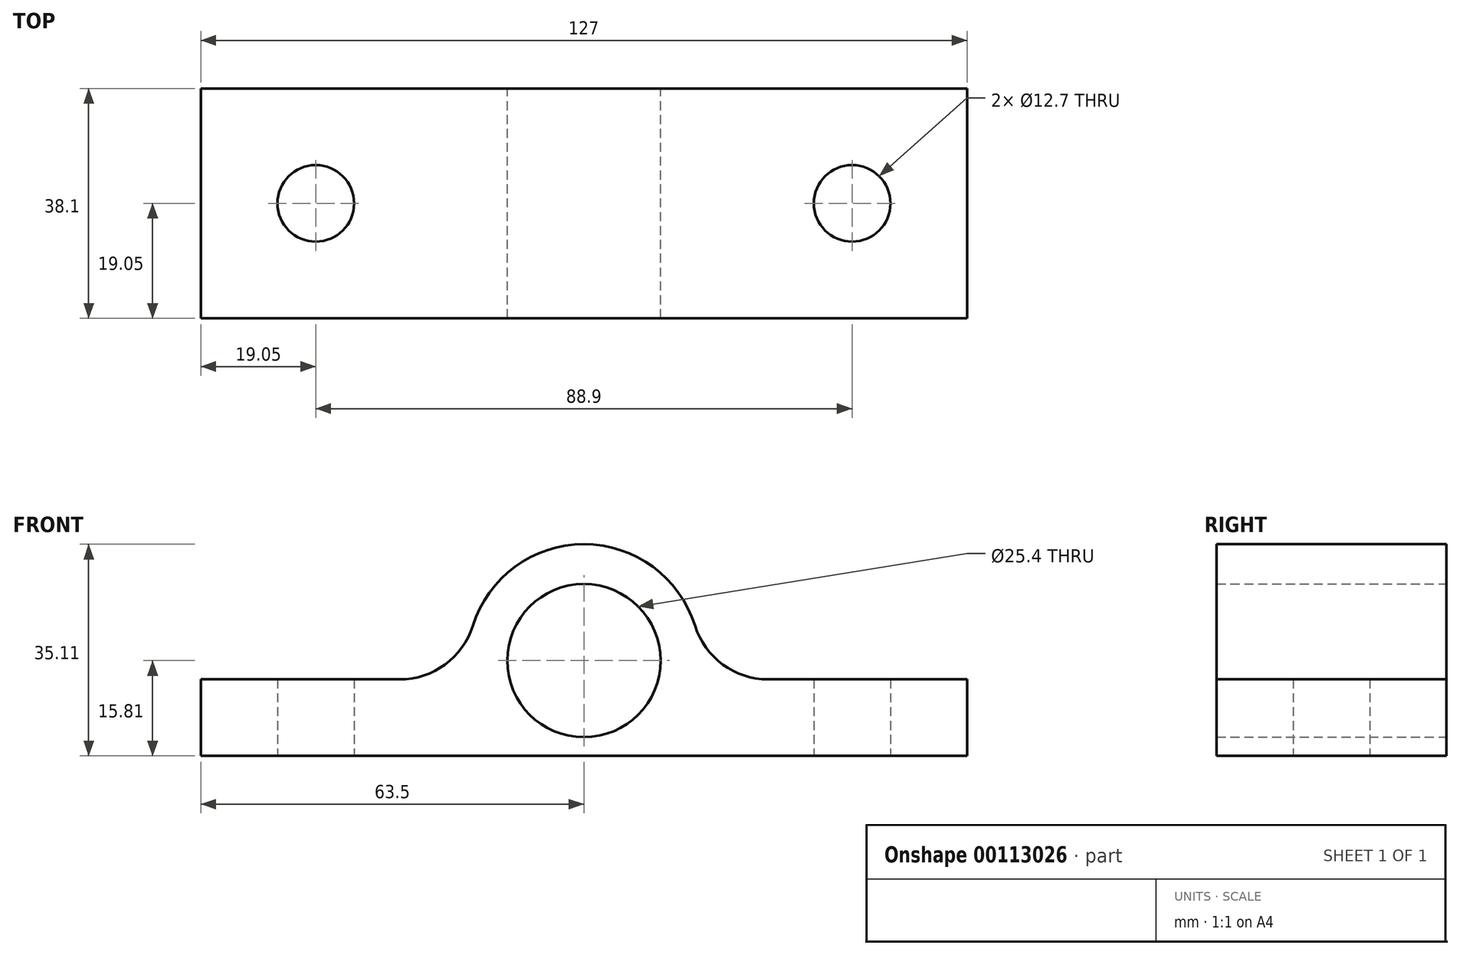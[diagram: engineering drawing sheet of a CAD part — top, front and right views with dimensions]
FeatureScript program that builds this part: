
annotation { "Feature Type Name" : "Feature", "Feature Type Description" : "" }
export const myFeature = defineFeature(function(context is Context, id is Id, definition is map)
    precondition{}
    {
        {
            var Q0;
            Q0=qCreatedBy(makeId("Front.planeOp"),FACE);
            var sketch = newSketch(context, id + "F0", { "sketchPlane" : qUnion([Q0])});
            skLineSegment(sketch, "E0", {"start": v(-63.5, 0) * mm, "end": v(63.5, 0) * mm});
            skLineSegment(sketch, "E1", {"start": v(63.5, 0) * mm, "end": v(63.5, 12.7) * mm});
            skLineSegment(sketch, "E2", {"start": v(63.5, 12.7) * mm, "end": v(19.05, 12.7) * mm});
            skLineSegment(sketch, "E3", {"start": v(-63.5, 0) * mm, "end": v(-63.5, 12.7) * mm});
            skLineSegment(sketch, "E4", {"start": v(-63.5, 12.7) * mm, "end": v(-19.05, 12.7) * mm});
            skArc(sketch, "E5", {"start": v(19.05, 12.7) * mm, "mid": v(0, 35.11) * mm, "end": v(-19.05, 12.7) * mm});
            skCircle(sketch, "E6", {"center": v(0, 15.81) * mm, "radius": 12.7 * mm});
            skSolve(sketch);
        }
        {
            var Q0;
            Q0=makeQuery(id+"F0.imprint","IMPRINT",FACE,{"disambiguationData":[TD([[makeQuery(id+"F0.imprint","IMPRINT",EDGE,{"derivedFrom":sQuery(id+"F0.wireOp",EDGE,"E0")}),1.0]])]});
            extrude(context, id + "F1", {"entities" : qUnion([Q0]), "endBound" : BoundingType.SYMMETRIC, "depth" : 38.1 * mm});
        }
        {
            var Q0;
            Q0=makeQuery(id+"F1.opExtrude","SWEPT_EDGE",EDGE,{"disambiguationData":[OSD([sQuery(id+"F0.wireOp",EDGE,"E4"),sQuery(id+"F0.wireOp",EDGE,"E5")])]});
            var Q1;
            Q1=makeQuery(id+"F1.opExtrude","SWEPT_EDGE",EDGE,{"disambiguationData":[OSD([sQuery(id+"F0.wireOp",EDGE,"E2"),sQuery(id+"F0.wireOp",EDGE,"E5")])]});
            fillet(context, id + "F2", {"entities" : qUnion([Q0, Q1]), "radius" : 12.7 * mm, "tangentPropagation" : true, "allowEdgeOverflow" : false});
        }
        {
            var Q0;
            Q0=makeQuery(id+"F1.opExtrude","SWEPT_FACE",FACE,{"disambiguationData":[OSD([sQuery(id+"F0.wireOp",EDGE,"E0")])]});
            var sketch = newSketch(context, id + "F3", { "sketchPlane" : qUnion([Q0])});
            skCircle(sketch, "E7", {"center": v(-44.45, 0) * mm, "radius": 6.35 * mm});
            skCircle(sketch, "E8", {"center": v(44.45, 0) * mm, "radius": 6.35 * mm});
            skSolve(sketch);
        }
        {
            var Q0;
            Q0=sQuery(id+"F3.wireOp",EDGE,"E7");
            var Q1;
            Q1=makeQuery(id+"F1.opExtrude","SWEPT_FACE",FACE,{"disambiguationData":[OSD([sQuery(id+"F0.wireOp",EDGE,"E4")])]});
            extrude(context, id + "F4", {"bodyType" : ToolBodyType.SURFACE, "surfaceEntities" : qUnion([Q0]), "endBound" : BoundingType.UP_TO_SURFACE, "oppositeDirection" : true, "endBoundEntityFace" : qUnion([Q1]), "depth" : 25.4 * mm});
        }
        {
            var Q0;
            Q0 = qSketchRegion(id + "F3", true);
            var Q1;
            Q1=makeQuery(id+"F1.opExtrude","SWEPT_FACE",FACE,{"disambiguationData":[OSD([sQuery(id+"F0.wireOp",EDGE,"E4")])]});
            extrude(context, id + "F5", {"entities" : qUnion([Q0]), "operationType" : NewBodyOperationType.REMOVE, "endBound" : BoundingType.UP_TO_SURFACE, "oppositeDirection" : true, "endBoundEntityFace" : qUnion([Q1]), "depth" : 25.4 * mm});
        }
    });
